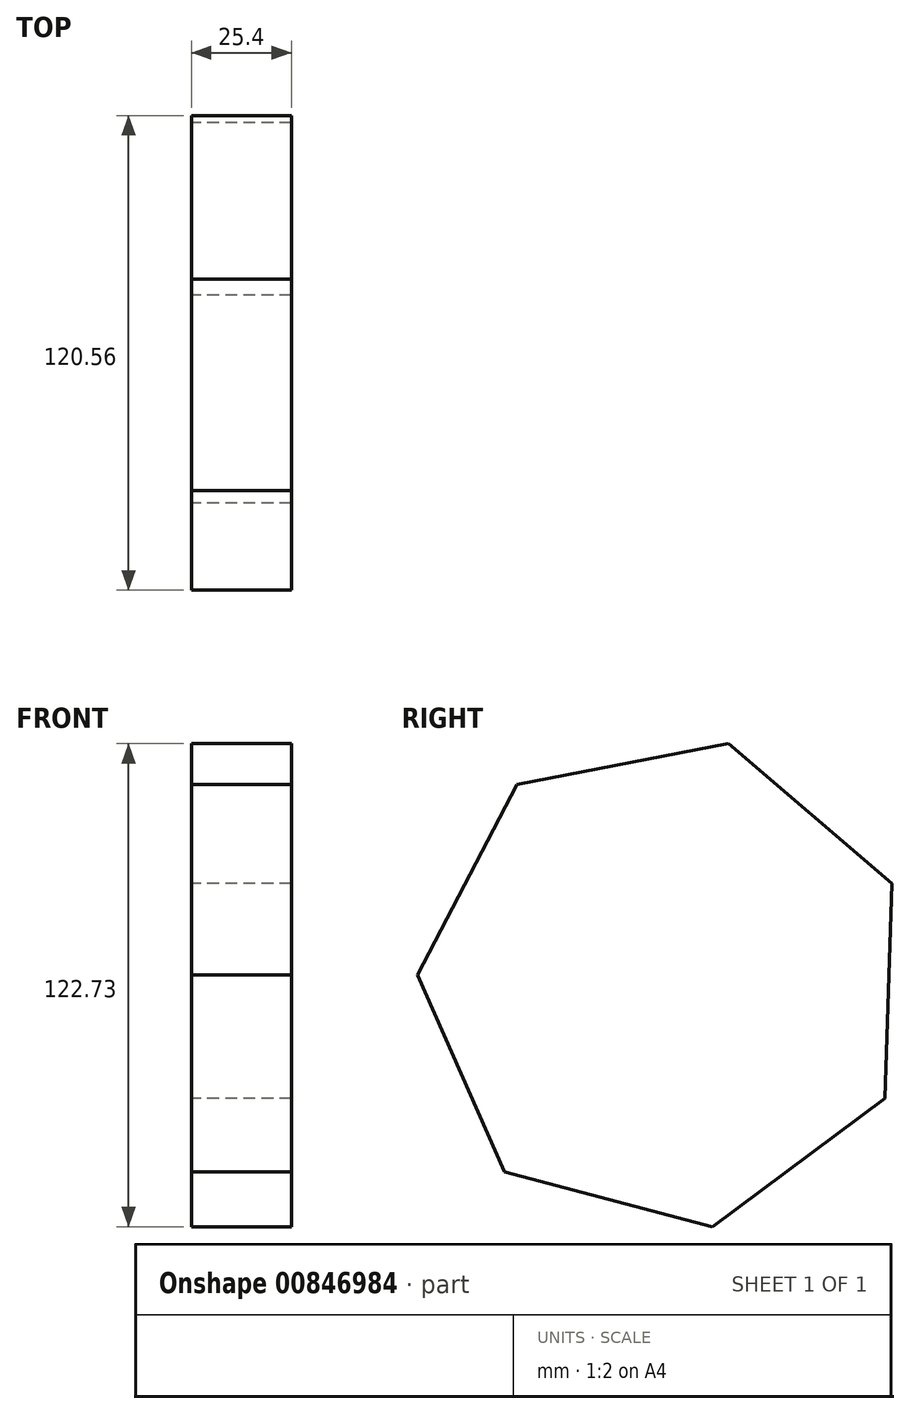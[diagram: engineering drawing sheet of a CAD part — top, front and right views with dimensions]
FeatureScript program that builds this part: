
annotation { "Feature Type Name" : "Feature", "Feature Type Description" : "" }
export const myFeature = defineFeature(function(context is Context, id is Id, definition is map)
    precondition{}
    {
        {
            var Q0;
            Q0=qCreatedBy(makeId("Right.planeOp"),FACE);
            var sketch = newSketch(context, id + "F0", { "sketchPlane" : qUnion([Q0])});
            skCircle(sketch, "E0.cCircle", {"center": v(0, 0) * mm, "radius": 62.98 * mm, "construction": true});
            skLineSegment(sketch, "E0.0", {"start": v(55.8, -29.2) * mm, "end": v(11.97, -61.83) * mm});
            skLineSegment(sketch, "E0.1", {"start": v(11.97, -61.83) * mm, "end": v(-40.88, -47.9) * mm});
            skLineSegment(sketch, "E0.2", {"start": v(-40.88, -47.9) * mm, "end": v(-62.94, 2.1) * mm});
            skLineSegment(sketch, "E0.3", {"start": v(-62.94, 2.1) * mm, "end": v(-37.6, 50.51) * mm});
            skLineSegment(sketch, "E0.4", {"start": v(-37.6, 50.51) * mm, "end": v(16.05, 60.9) * mm});
            skLineSegment(sketch, "E0.5", {"start": v(16.05, 60.9) * mm, "end": v(57.62, 25.43) * mm});
            skLineSegment(sketch, "E0.6", {"start": v(57.62, 25.43) * mm, "end": v(55.8, -29.2) * mm});
            skSolve(sketch);
        }
        {
            var Q0;
            Q0=makeQuery(id+"F0.imprint","IMPRINT",FACE,{"disambiguationData":[TD([[makeQuery(id+"F0.imprint","IMPRINT",EDGE,{"derivedFrom":sQuery(id+"F0.wireOp",EDGE,"E0.0")}),-1.0]])]});
            extrude(context, id + "F1", {"entities" : qUnion([Q0]), "depth" : 25.4 * mm, "offsetDistance" : 25.4 * mm});
        }
    });
